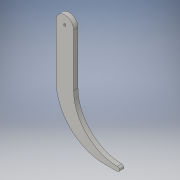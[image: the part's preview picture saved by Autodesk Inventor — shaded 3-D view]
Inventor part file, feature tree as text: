
AUTODESK INVENTOR PART (.ipt)
format: ipt  version: 2016 (Build 200138000, 138)  size: 107,008 bytes
history: native  units: in
note: dims shown in document units (in); Inventor stores cm internally (conversion verified against a paired STEP export)
features: extrude x1, sketch x1
ambient origin geometry x8: Origin, YZ Plane, XZ Plane, XY Plane, X Axis, Y Axis, Z Axis, Center Point
bodies: Body1 (feature_tree)
feature tree (2):
  extrude  "Extrusion2"  Depth=0.25in
  sketch  "Sketch1"  dims[d21=0.5in d22=0.0in d23=0.25in d24=2.0in d25=1.0in d26=5.0in d27=5.5in d28=6.0in d29=6.0in d30=0.25in d31=1.5in]
